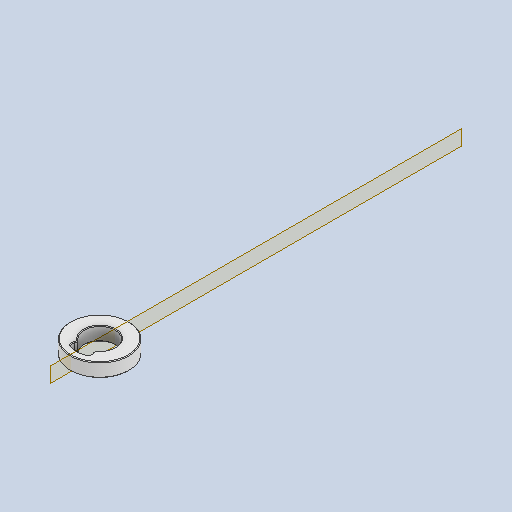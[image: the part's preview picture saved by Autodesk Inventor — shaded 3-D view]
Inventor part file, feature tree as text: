
AUTODESK INVENTOR PART (.ipt)
format: ipt  version: 2022 (Build 260153000, 153)  size: 147,968 bytes
history: native  units: in
note: dims shown in document units (in); Inventor stores cm internally (conversion verified against a paired STEP export)
features: sketch x1, other x1, plane x1, projected_geometry x1
ambient origin geometry x8: Origin, YZ Plane, XZ Plane, XY Plane, X Axis, Y Axis, Z Axis, Center Point
bodies: Solid1 (feature_tree), Body1 (feature_tree)
feature tree (4):
  sketch  "Sketch1"  dims[d0=90.0deg]
  other  "Work Axis1"
  plane  "Work Plane1"
  projected_geometry  "Projected Loop1"
